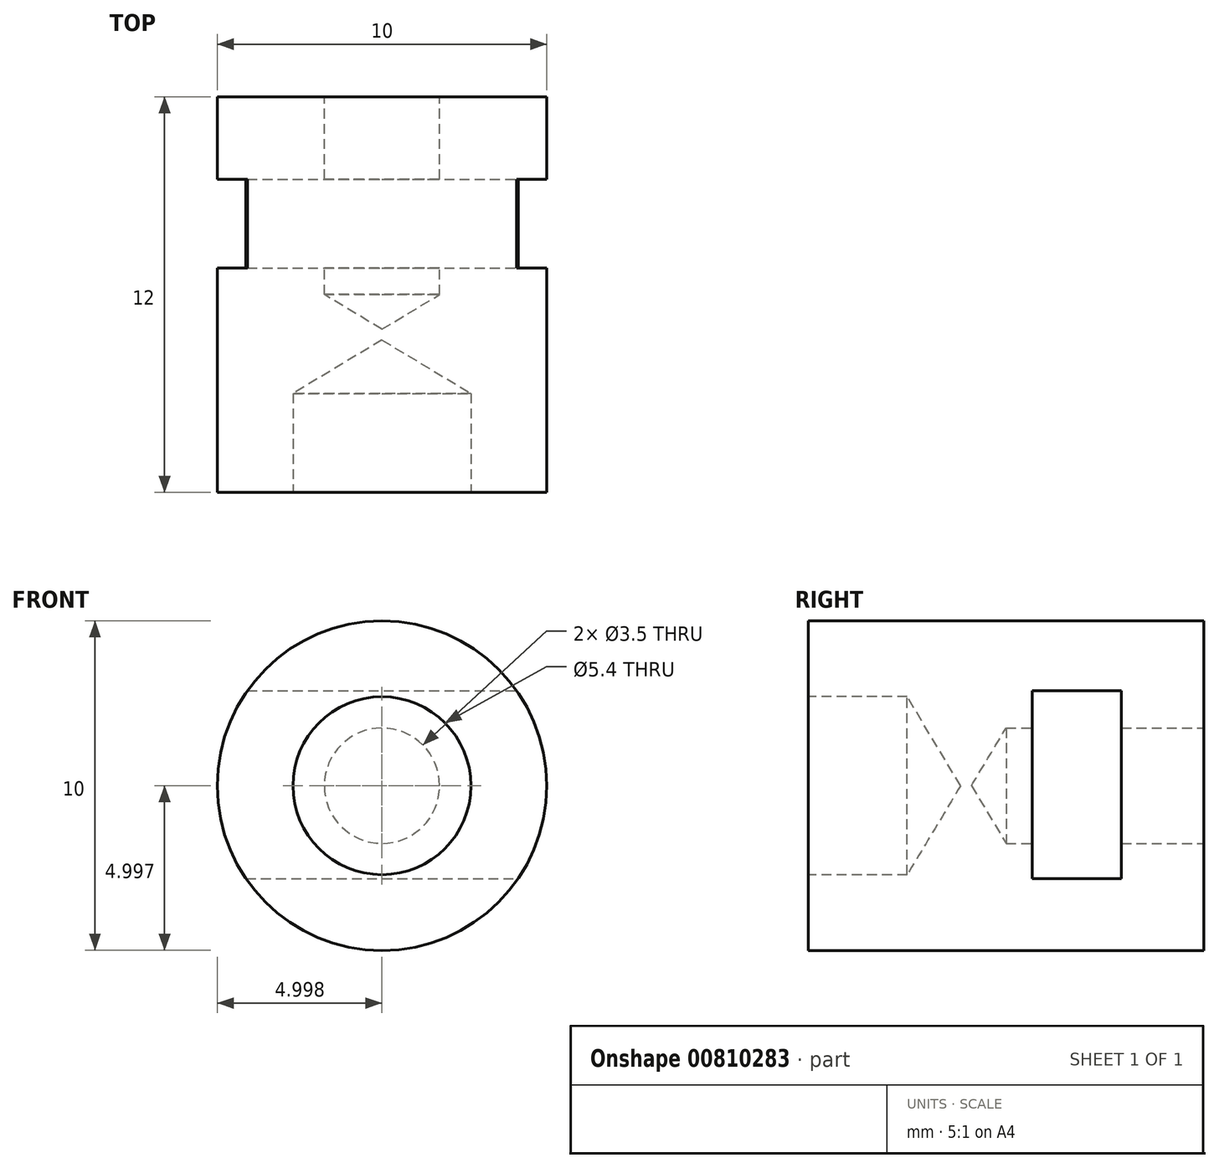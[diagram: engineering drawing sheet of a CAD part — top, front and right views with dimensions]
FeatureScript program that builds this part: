
annotation { "Feature Type Name" : "Feature", "Feature Type Description" : "" }
export const myFeature = defineFeature(function(context is Context, id is Id, definition is map)
    precondition{}
    {
        {
            assignVariable(context, id + "F0", {"name" : "BlowerCapHeadW", "anyValue" : 5.4});
        }
        {
            assignVariable(context, id + "F1", {"name" : "BlowerCapHeadH", "anyValue" : 3});
        }
        {
            assignVariable(context, id + "F2", {"name" : "AdaptorH", "anyValue" : 12});
        }
        {
            var Q0;
            Q0=qCreatedBy(makeId("Front.planeOp"),FACE);
            var sketch = newSketch(context, id + "F3", { "sketchPlane" : qUnion([Q0])});
            skLineSegment(sketch, "E0", {"start": v(-26.2, 28.5) * mm, "end": v(-40.65, 28.5) * mm, "construction": true});
            skLineSegment(sketch, "E1", {"start": v(-33.42, 35.73) * mm, "end": v(-33.42, 21.28) * mm, "construction": true});
            skPoint(sketch, "E2", {"position": v(-33.42, 28.5) * mm});
            skCircle(sketch, "E3", {"center": v(-33.42, 28.5) * mm, "radius": 5 * mm});
            skSolve(sketch);
        }
        {
            var Q0;
            Q0=makeQuery(id+"F3.imprint","IMPRINT",FACE,{"disambiguationData":[TD([[makeQuery(id+"F3.imprint","IMPRINT",EDGE,{"derivedFrom":sQuery(id+"F3.wireOp",EDGE,"E3")}),1.0]])]});
            extrude(context, id + "F4", {"entities" : qUnion([Q0]), "oppositeDirection" : true, "depth" : (getVariable(context, 'AdaptorH')) * mm, "offsetDistance" : 25 * mm});
        }
        {
            var Q0;
            Q0=makeQuery(id+"F4.opExtrude","CAP_FACE",FACE,{"disambiguationData":[OSD([sQuery(id+"F3.wireOp",EDGE,"E3")])],"isStart":false});
            var sketch = newSketch(context, id + "F5", { "sketchPlane" : qUnion([Q0])});
            skPoint(sketch, "E4.0", {"position": v(33.42, 28.5) * mm});
            skSolve(sketch);
        }
        {
            var Q0;
            Q0=sQuery(id+"F3.wireOp",VERTEX,"E2");
            var Q1;
            Q1=makeQuery(id+"F4.opExtrude","SWEPT_BODY",BODY,{"disambiguationData":[OSD([sQuery(id+"F3.wireOp",EDGE,"E3")])]});
            hole(context, id + "F6", {"style" : HoleStyle.SIMPLE, "endStyle" : HoleEndStyle.BLIND, "holeDiameter" : (getVariable(context, 'BlowerCapHeadW')) * mm, "majorDiameter" : 5 * mm, "holeDepth" : (getVariable(context, 'BlowerCapHeadH')) * mm, "isTappedThrough" : true, "tappedDepth" : 6.5 * mm, "tapClearance" : 3, "startFromSketch" : true, "locations" : qUnion([Q0]), "scope" : qUnion([Q1])});
        }
        {
            var Q0;
            Q0=sQuery(id+"F5.wireOp",VERTEX,"E4.0");
            var Q1;
            Q1=makeQuery(id+"F4.opExtrude","SWEPT_BODY",BODY,{"disambiguationData":[OSD([sQuery(id+"F3.wireOp",EDGE,"E3")])]});
            hole(context, id + "F7", {"style" : HoleStyle.SIMPLE, "endStyle" : HoleEndStyle.BLIND, "holeDiameter" : 3.5 * mm, "majorDiameter" : 5 * mm, "holeDepth" : 6 * mm, "isTappedThrough" : true, "tappedDepth" : 6.5 * mm, "tapClearance" : 3, "startFromSketch" : true, "locations" : qUnion([Q0]), "scope" : qUnion([Q1])});
        }
        {
            var Q0;
            Q0=qCreatedBy(makeId("Right.planeOp"),FACE);
            var sketch = newSketch(context, id + "F8", { "sketchPlane" : qUnion([Q0])});
            skPoint(sketch, "E5.0", {"position": v(0, 28.5) * mm});
            skPoint(sketch, "E6.0", {"position": v(12, 28.5) * mm});
            skLineSegment(sketch, "E7", {"start": v(0, 28.5) * mm, "end": v(12, 28.5) * mm, "construction": true});
            skLineSegment(sketch, "E8", {"start": v(8.15, 30.47) * mm, "end": v(8.15, 26.61) * mm, "construction": true});
            skPoint(sketch, "E9", {"position": v(8.15, 28.54) * mm});
            skLineSegment(sketch, "E10.bottom", {"start": v(9.5, 25.7) * mm, "end": v(6.8, 25.7) * mm});
            skLineSegment(sketch, "E10.top", {"start": v(9.5, 31.4) * mm, "end": v(6.8, 31.4) * mm});
            skLineSegment(sketch, "E10.left", {"start": v(9.5, 25.7) * mm, "end": v(9.5, 31.4) * mm});
            skLineSegment(sketch, "E10.right", {"start": v(6.8, 25.7) * mm, "end": v(6.8, 31.4) * mm});
            skSolve(sketch);
        }
        {
            var Q0;
            Q0=qSketchRegion(id+"F8",true);
            extrude(context, id + "F9", {"entities" : qUnion([Q0]), "operationType" : NewBodyOperationType.REMOVE, "endBound" : BoundingType.THROUGH_ALL, "oppositeDirection" : true, "depth" : 25 * mm, "offsetDistance" : 25 * mm});
        }
    });
